# Revit family: Chair_Task_Schiavello_Dash
name_source: partatom
category: Furniture
units: mm (PartAtom-declared; Revit-internal decimal feet)

## family parameters
Always vertical = Yes
Cut with Voids When Loaded = No
OmniClass Number = 23.21.13.00
OmniClass Title = Retail and Office Equipment and Furnishings
Room Calculation Point = No
Shared = No
Work Plane-Based = No

## types (2) — shared parameters
Assembly Code = E2020200
Description = Presenting an attractive curved frame and a variety of smooth finish options, Dash is an adaptable task chair for any environment and any body type. Feature packed with standard seat depth adjustment, a weight activated auto-balance mechanism and self-adjusting lumbar support, Dash comfortable and intuitive.
IfcExportAs = IfcFurniture
IfcExportType = CHAIR
Manufacturer = Schiavello
ManufacturerOverallDepth = 670 mm
ManufacturerURLProductSpecific = https://www.schiavello.com
ModifiedIssue = 20230127 $
URL = https://www.schiavello.com
Uniclass2015Code = Pr_40_50_12_57
Uniclass2015Title = Office chairs
Uniclass2015Version = Products v1.24

## per-type parameters (varying)
| type | ArmRest | ManufacturerOverallWidth | ManufacturerSpecCode | Model | NoArmRest | Type Comments |
| 670w x 670d x 990h_No Arm (DATA430NA) | No | 670 mm | Dash Chair - 670w x 670d x 990h - No Arm | Dash Chair - 670w x 670d x 990h - No Arm | Yes | 670w x 670d x 990h - No Arm |
| 740w x 670d x 990h_With Arm (DATA430AA) | Yes | 740 mm | Dash Chair - 740w x 670d x 990h - With Arm | Dash Chair - 740w x 670d x 990h - With Arm | No | 740w x 670d x 990h - With Arm |

## geometry (parser evidence)
native form markers: Sweep x2
no freeform markers — native parametric forms only
